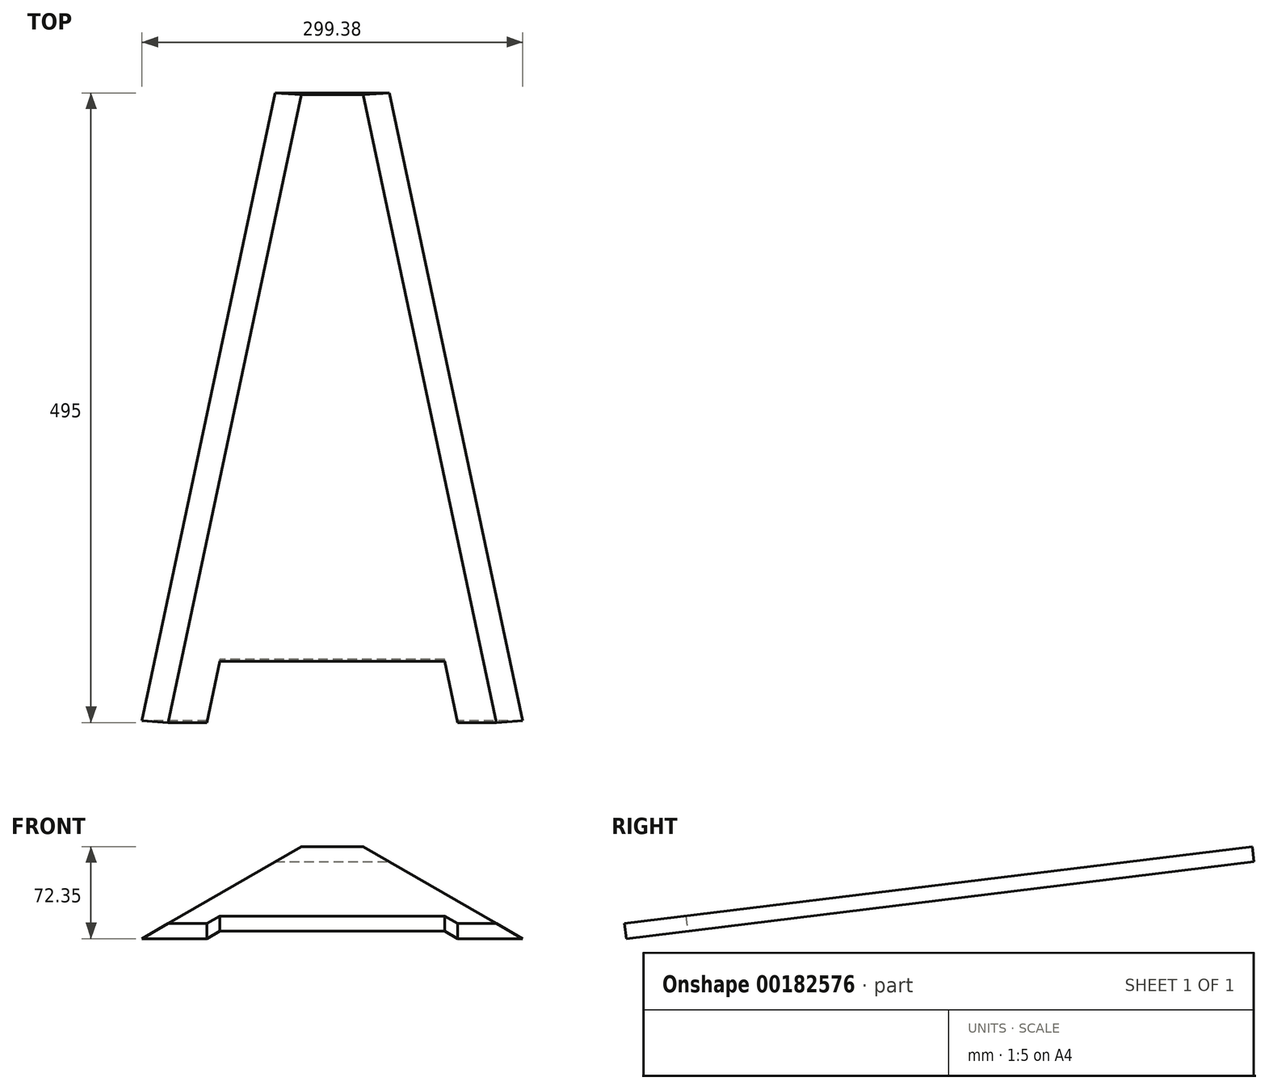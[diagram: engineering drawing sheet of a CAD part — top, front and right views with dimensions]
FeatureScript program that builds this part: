
annotation { "Feature Type Name" : "Feature", "Feature Type Description" : "" }
export const myFeature = defineFeature(function(context is Context, id is Id, definition is map)
    precondition{}
    {
        {
            var Q0;
            Q0=qCreatedBy(makeId("Top.planeOp"),FACE);
            var sketch = newSketch(context, id + "F0", { "sketchPlane" : qUnion([Q0])});
            skLineSegment(sketch, "E0", {"start": v(-150, 0) * mm, "end": v(150, 0) * mm, "construction": true});
            skLineSegment(sketch, "E1", {"start": v(0, 0) * mm, "end": v(0, 495) * mm, "construction": true});
            skLineSegment(sketch, "E2", {"start": v(-45, 495) * mm, "end": v(45, 495) * mm, "construction": true});
            skSolve(sketch);
        }
        {
            var Q0;
            Q0=qCreatedBy(makeId("Front.planeOp"),FACE);
            var sketch = newSketch(context, id + "F1", { "sketchPlane" : qUnion([Q0])});
            skCircle(sketch, "E3.cCircle", {"center": v(0, 0) * mm, "radius": 86.6 * mm, "construction": true});
            skLineSegment(sketch, "E3.0", {"start": v(150, -86.6) * mm, "end": v(-150, -86.6) * mm});
            skLineSegment(sketch, "E3.1", {"start": v(-150, -86.6) * mm, "end": v(0, 173.2) * mm});
            skLineSegment(sketch, "E3.2", {"start": v(0, 173.2) * mm, "end": v(150, -86.6) * mm});
            skPoint(sketch, "E3.0.midPoint", {"position": v(0, -86.6) * mm});
            skSolve(sketch);
        }
        {
            var Q0;
            Q0=sQuery(id+"F0.wireOp",EDGE,"E2");
            cPoint(context, id + "F2", {"entities" : qUnion([Q0]), "parameter" : 0.5});
        }
        {
            var Q0;
            Q0=qCreatedBy(id+"F2",VERTEX);
            var Q1;
            Q1=sQuery(id+"F0.wireOp",EDGE,"E1");
            cPlane(context, id + "F3", {"entities" : qUnion([Q0, Q1]), "cplaneType" : CPlaneType.LINE_POINT, "offset" : 25 * mm, "width" : 150 * mm, "height" : 150 * mm});
        }
        {
            var Q0;
            Q0=qCreatedBy(id+"F3.planeOp",FACE);
            var sketch = newSketch(context, id + "F4", { "sketchPlane" : qUnion([Q0])});
            skCircle(sketch, "E4.cCircle", {"center": v(0, 0) * mm, "radius": 25.98 * mm, "construction": true});
            skLineSegment(sketch, "E4.0", {"start": v(45, -25.98) * mm, "end": v(-45, -25.98) * mm});
            skLineSegment(sketch, "E4.1", {"start": v(-45, -25.98) * mm, "end": v(0, 51.96) * mm});
            skLineSegment(sketch, "E4.2", {"start": v(0, 51.96) * mm, "end": v(45, -25.98) * mm});
            skPoint(sketch, "E4.0.midPoint", {"position": v(0, -25.98) * mm});
            skSolve(sketch);
        }
        {
            var Q0;
            Q0=makeQuery(id+"F1.imprint","IMPRINT",FACE,{"disambiguationData":[TD([[makeQuery(id+"F1.imprint","IMPRINT",EDGE,{"derivedFrom":sQuery(id+"F1.wireOp",EDGE,"E3.0")}),-1.0]])]});
            var Q1;
            Q1=makeQuery(id+"F4.imprint","IMPRINT",FACE,{"disambiguationData":[TD([[makeQuery(id+"F4.imprint","IMPRINT",EDGE,{"derivedFrom":sQuery(id+"F4.wireOp",EDGE,"E4.0")}),-1.0]])]});
            loft(context, id + "F5", {"sheetProfilesArray" : [{ "sheetProfileEntities" : qUnion([Q0]) }, { "sheetProfileEntities" : qUnion([Q1]) }]});
        }
        {
            var Q0;
            {var subQ0=sQuery(id+"F4.wireOp",EDGE,"E4.0");var subQ1=sQuery(id+"F4.wireOp",EDGE,"E4.1");var subQ2=sQuery(id+"F4.wireOp",EDGE,"E4.2");var subQ3=sQuery(id+"F1.wireOp",EDGE,"E3.0");var subQ4=sQuery(id+"F1.wireOp",EDGE,"E3.1");var subQ5=sQuery(id+"F1.wireOp",EDGE,"E3.2");Q0=makeQuery(id+"F5.opLoft","SWEPT_FACE",FACE,{"disambiguationData":[OSD([subQ3,subQ4,subQ5,subQ0,subQ1,subQ2]),TDD([makeQuery(id+"F1.imprint","INTERSECT",VERTEX,{"derivedFrom":[subQ3,subQ5]}),makeQuery(id+"F1.imprint","INTERSECT",VERTEX,{"derivedFrom":[subQ3,subQ4]}),makeQuery(id+"F1.imprint","IMPRINT",EDGE,{"derivedFrom":subQ3}),makeQuery(id+"F4.imprint","INTERSECT",VERTEX,{"derivedFrom":[subQ0,subQ2]}),makeQuery(id+"F4.imprint","INTERSECT",VERTEX,{"derivedFrom":[subQ0,subQ1]}),makeQuery(id+"F4.imprint","IMPRINT",EDGE,{"derivedFrom":subQ0})])]});}
            cPlane(context, id + "F6", {"entities" : qUnion([Q0]), "cplaneType" : CPlaneType.OFFSET, "offset" : 12 * mm, "oppositeDirection" : true, "width" : 150 * mm, "height" : 150 * mm});
        }
        {
            var Q0;
            Q0=qCreatedBy(id+"F6.planeOp",FACE);
            var sketch = newSketch(context, id + "F7", { "sketchPlane" : qUnion([Q0])});
            skCircle(sketch, "E5", {"center": v(0, -288.01) * mm, "radius": 411.12 * mm});
            skSolve(sketch);
        }
        {
            var Q0;
            Q0 = qSketchRegion(id + "F7", true);
            extrude(context, id + "F8", {"entities" : qUnion([Q0]), "operationType" : NewBodyOperationType.REMOVE, "endBound" : BoundingType.THROUGH_ALL, "oppositeDirection" : true, "depth" : 25 * mm});
        }
        {
            var Q0;
            {var subQ0=sQuery(id+"F4.wireOp",EDGE,"E4.0");var subQ1=sQuery(id+"F4.wireOp",EDGE,"E4.1");var subQ2=sQuery(id+"F4.wireOp",EDGE,"E4.2");var subQ3=sQuery(id+"F1.wireOp",EDGE,"E3.0");var subQ4=sQuery(id+"F1.wireOp",EDGE,"E3.1");var subQ5=sQuery(id+"F1.wireOp",EDGE,"E3.2");Q0=makeQuery(id+"F5.opLoft","SWEPT_FACE",FACE,{"disambiguationData":[OSD([subQ3,subQ4,subQ5,subQ0,subQ1,subQ2]),TDD([makeQuery(id+"F1.imprint","INTERSECT",VERTEX,{"derivedFrom":[subQ3,subQ5]}),makeQuery(id+"F1.imprint","INTERSECT",VERTEX,{"derivedFrom":[subQ3,subQ4]}),makeQuery(id+"F1.imprint","IMPRINT",EDGE,{"derivedFrom":subQ3}),makeQuery(id+"F4.imprint","INTERSECT",VERTEX,{"derivedFrom":[subQ0,subQ2]}),makeQuery(id+"F4.imprint","INTERSECT",VERTEX,{"derivedFrom":[subQ0,subQ1]}),makeQuery(id+"F4.imprint","IMPRINT",EDGE,{"derivedFrom":subQ0})])]});}
            var sketch = newSketch(context, id + "F9", { "sketchPlane" : qUnion([Q0])});
            skLineSegment(sketch, "E6", {"start": v(98.9, 10.53) * mm, "end": v(88.38, -39.47) * mm});
            skLineSegment(sketch, "E7", {"start": v(88.38, -39.47) * mm, "end": v(-88.38, -39.47) * mm});
            skLineSegment(sketch, "E8", {"start": v(-88.38, -39.47) * mm, "end": v(-98.9, 10.53) * mm});
            skLineSegment(sketch, "E9", {"start": v(98.9, 10.53) * mm, "end": v(-98.9, 10.53) * mm});
            skSolve(sketch);
        }
        {
            var Q0;
            Q0 = qSketchRegion(id + "F9", true);
            extrude(context, id + "F10", {"entities" : qUnion([Q0]), "operationType" : NewBodyOperationType.REMOVE, "endBound" : BoundingType.THROUGH_ALL, "oppositeDirection" : true, "depth" : 25 * mm});
        }
        {
            var Q0;
            Q0=makeQuery(id+"F5.opLoft","CAP_FACE",FACE,{"disambiguationData":[OSD([makeQuery(id+"F4.imprint","IMPRINT",FACE,{"disambiguationData":[TD([[makeQuery(id+"F4.imprint","IMPRINT",EDGE,{"derivedFrom":sQuery(id+"F4.wireOp",EDGE,"E4.0")}),-1.0]])]})])],"isStart":true});
            var sketch = newSketch(context, id + "F11", { "sketchPlane" : qUnion([Q0])});
            skLineSegment(sketch, "E10", {"start": v(45, -25.98) * mm, "end": v(24.06, -13.9) * mm});
            skLineSegment(sketch, "E11", {"start": v(-45, -25.98) * mm, "end": v(-24.06, -13.9) * mm});
            skSolve(sketch);
        }
        {
            var Q0;
            Q0=makeQuery(id+"F5.opLoft","SWEPT_EDGE",EDGE,{"disambiguationData":[OSD([sQuery(id+"F1.wireOp",EDGE,"E3.0"),sQuery(id+"F1.wireOp",EDGE,"E3.1"),sQuery(id+"F4.wireOp",EDGE,"E4.0"),sQuery(id+"F4.wireOp",EDGE,"E4.2")])]});
            var Q1;
            Q1=sQuery(id+"F11.wireOp",EDGE,"E10");
            cPlane(context, id + "F12", {"entities" : qUnion([Q0, Q1]), "cplaneType" : CPlaneType.LINE_ANGLE, "offset" : 25 * mm, "angle" : 0 * degree, "width" : 150 * mm, "height" : 150 * mm});
        }
        {
            var Q0;
            Q0=qCreatedBy(id+"F12.planeOp",FACE);
            var sketch = newSketch(context, id + "F13", { "sketchPlane" : qUnion([Q0])});
            skCircle(sketch, "E12", {"center": v(-100.1, -240.25) * mm, "radius": 303.08 * mm});
            skSolve(sketch);
        }
        {
            var Q0;
            Q0 = qSketchRegion(id + "F13", true);
            extrude(context, id + "F14", {"entities" : qUnion([Q0]), "operationType" : NewBodyOperationType.REMOVE, "endBound" : BoundingType.THROUGH_ALL, "oppositeDirection" : true, "depth" : 25 * mm});
        }
        {
            var Q0;
            Q0=sQuery(id+"F11.wireOp",EDGE,"E11");
            var Q1;
            Q1=makeQuery(id+"F5.opLoft","SWEPT_EDGE",EDGE,{"disambiguationData":[OSD([sQuery(id+"F1.wireOp",EDGE,"E3.0"),sQuery(id+"F1.wireOp",EDGE,"E3.2"),sQuery(id+"F4.wireOp",EDGE,"E4.0"),sQuery(id+"F4.wireOp",EDGE,"E4.1")])]});
            cPlane(context, id + "F15", {"entities" : qUnion([Q0, Q1]), "cplaneType" : CPlaneType.LINE_ANGLE, "offset" : 25 * mm, "angle" : 0 * degree, "width" : 150 * mm, "height" : 150 * mm});
        }
        {
            var Q0;
            Q0=qCreatedBy(id+"F15.planeOp",FACE);
            var sketch = newSketch(context, id + "F16", { "sketchPlane" : qUnion([Q0])});
            skCircle(sketch, "E13", {"center": v(93.33, -267.97) * mm, "radius": 347.38 * mm});
            skSolve(sketch);
        }
        {
            var Q0;
            Q0 = qSketchRegion(id + "F16", true);
            extrude(context, id + "F17", {"entities" : qUnion([Q0]), "operationType" : NewBodyOperationType.REMOVE, "endBound" : BoundingType.THROUGH_ALL, "oppositeDirection" : true, "depth" : 25 * mm});
        }
        {
            var Q0;
            {var subQ0=sQuery(id+"F4.wireOp",EDGE,"E4.0");var subQ1=sQuery(id+"F4.wireOp",EDGE,"E4.1");var subQ2=sQuery(id+"F4.wireOp",EDGE,"E4.2");var subQ3=sQuery(id+"F1.wireOp",EDGE,"E3.0");var subQ4=sQuery(id+"F1.wireOp",EDGE,"E3.1");var subQ5=sQuery(id+"F1.wireOp",EDGE,"E3.2");Q0=makeQuery(id+"F5.opLoft","SWEPT_FACE",FACE,{"disambiguationData":[OSD([subQ3,subQ4,subQ5,subQ0,subQ1,subQ2]),TDD([makeQuery(id+"F1.imprint","INTERSECT",VERTEX,{"derivedFrom":[subQ3,subQ5]}),makeQuery(id+"F1.imprint","INTERSECT",VERTEX,{"derivedFrom":[subQ3,subQ4]}),makeQuery(id+"F1.imprint","IMPRINT",EDGE,{"derivedFrom":subQ3}),makeQuery(id+"F4.imprint","INTERSECT",VERTEX,{"derivedFrom":[subQ0,subQ2]}),makeQuery(id+"F4.imprint","INTERSECT",VERTEX,{"derivedFrom":[subQ0,subQ1]}),makeQuery(id+"F4.imprint","IMPRINT",EDGE,{"derivedFrom":subQ0})])]});}
            var sketch = newSketch(context, id + "F18", { "sketchPlane" : qUnion([Q0])});
            skLineSegment(sketch, "E14.bottom", {"start": v(45, -488.17) * mm, "end": v(-45, -488.17) * mm});
            skLineSegment(sketch, "E14.top", {"start": v(45, -523.53) * mm, "end": v(-45, -523.53) * mm});
            skLineSegment(sketch, "E14.left", {"start": v(45, -488.17) * mm, "end": v(45, -523.53) * mm});
            skLineSegment(sketch, "E14.right", {"start": v(-45, -488.17) * mm, "end": v(-45, -523.53) * mm});
            skSolve(sketch);
        }
        {
            var Q0;
            Q0 = qSketchRegion(id + "F18", true);
            extrude(context, id + "F19", {"entities" : qUnion([Q0]), "operationType" : NewBodyOperationType.REMOVE, "endBound" : BoundingType.THROUGH_ALL, "oppositeDirection" : true, "depth" : 25 * mm});
        }
        {
            var Q0;
            Q0=makeQuery(id+"F8.boolean.opBoolean","COPY",FACE,{"derivedFrom":makeQuery(id+"F8.opExtrude","CAP_FACE",FACE,{"disambiguationData":[OSD([sQuery(id+"F7.wireOp",EDGE,"E5")])],"isStart":true})});
            var sketch = newSketch(context, id + "F20", { "sketchPlane" : qUnion([Q0])});
            skLineSegment(sketch, "E15.bottom", {"start": v(-177.88, -9.06) * mm, "end": v(200.17, -9.06) * mm});
            skLineSegment(sketch, "E15.top", {"start": v(-177.88, -60.76) * mm, "end": v(200.17, -60.76) * mm});
            skLineSegment(sketch, "E15.left", {"start": v(-177.88, -9.06) * mm, "end": v(-177.88, -60.76) * mm});
            skLineSegment(sketch, "E15.right", {"start": v(200.17, -9.06) * mm, "end": v(200.17, -60.76) * mm});
            skSolve(sketch);
        }
        {
            var Q0;
            Q0 = qSketchRegion(id + "F20", true);
            extrude(context, id + "F21", {"entities" : qUnion([Q0]), "operationType" : NewBodyOperationType.REMOVE, "endBound" : BoundingType.THROUGH_ALL, "oppositeDirection" : true, "depth" : 25 * mm});
        }
    });
